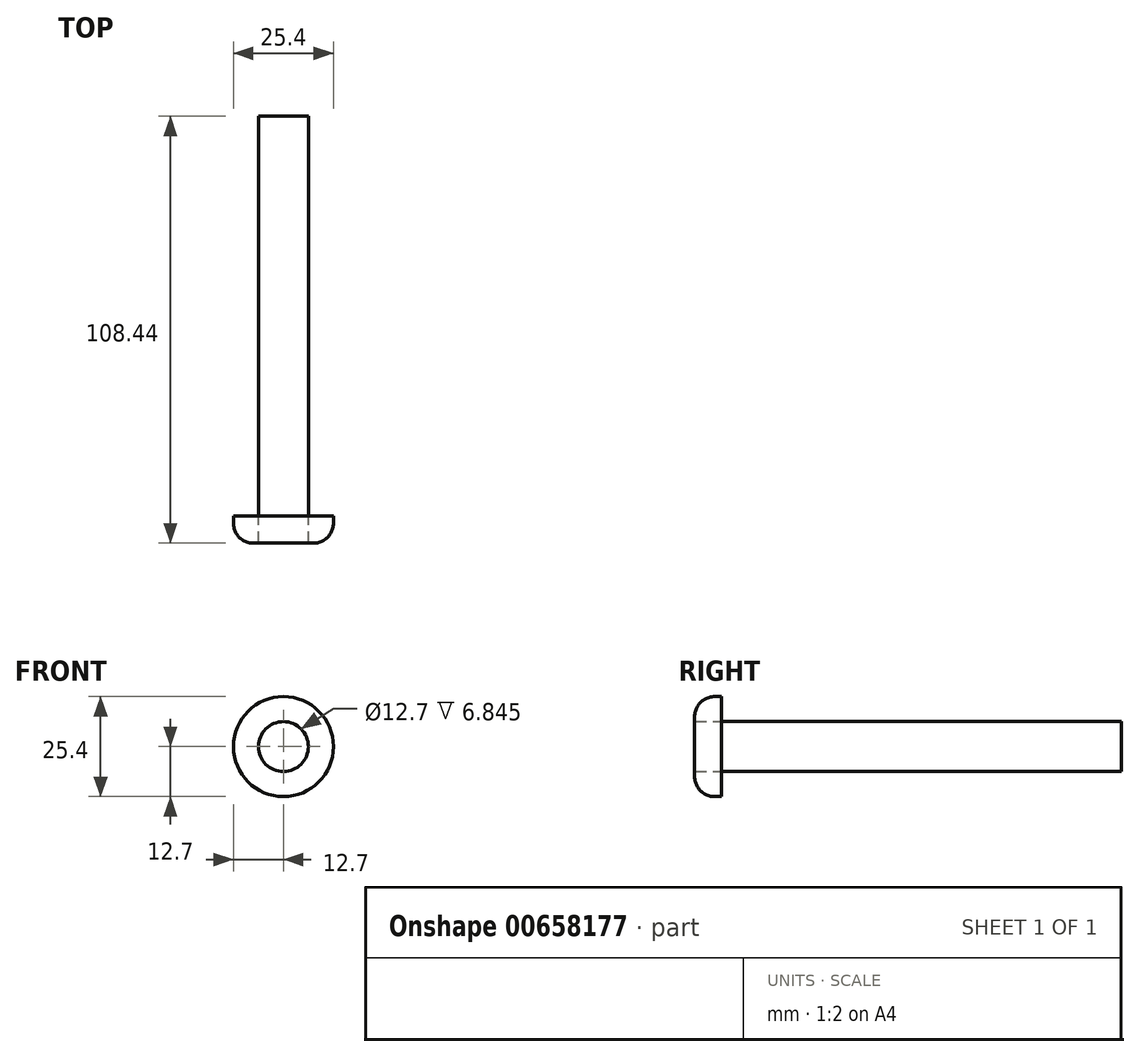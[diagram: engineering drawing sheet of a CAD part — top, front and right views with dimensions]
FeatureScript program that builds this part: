
annotation { "Feature Type Name" : "Feature", "Feature Type Description" : "" }
export const myFeature = defineFeature(function(context is Context, id is Id, definition is map)
    precondition{}
    {
        {
            var Q0;
            Q0=qCreatedBy(makeId("Front.planeOp"),FACE);
            var sketch = newSketch(context, id + "F0", { "sketchPlane" : qUnion([Q0])});
            skCircle(sketch, "E0", {"center": v(0, 0) * mm, "radius": 6.35 * mm});
            skCircle(sketch, "E1", {"center": v(0, 0) * mm, "radius": 12.7 * mm});
            skSolve(sketch);
        }
        {
            var Q0;
            Q0=makeQuery(id+"F0.imprint","IMPRINT",FACE,{"disambiguationData":[TD([[makeQuery(id+"F0.imprint","IMPRINT",EDGE,{"derivedFrom":sQuery(id+"F0.wireOp",EDGE,"E0")}),-1.0]])]});
            extrude(context, id + "F1", {"entities" : qUnion([Q0]), "depth" : 6.84 * mm, "offsetDistance" : 25.4 * mm});
        }
        {
            var Q0;
            Q0=makeQuery(id+"F1.opExtrude","CAP_EDGE",EDGE,{"disambiguationData":[OSD([sQuery(id+"F0.wireOp",EDGE,"E1")])],"isStart":false});
            fillet(context, id + "F2", {"entities" : qUnion([Q0]), "radius" : 5.08 * mm, "tangentPropagation" : true, "allowEdgeOverflow" : false});
        }
        {
            var Q0;
            Q0=makeQuery(id+"F0.imprint","IMPRINT",FACE,{"disambiguationData":[TD([[makeQuery(id+"F0.imprint","IMPRINT",EDGE,{"derivedFrom":sQuery(id+"F0.wireOp",EDGE,"E0")}),1.0]])]});
            extrude(context, id + "F3", {"entities" : qUnion([Q0]), "oppositeDirection" : true, "depth" : 101.6 * mm, "offsetDistance" : 25.4 * mm});
        }
    });
